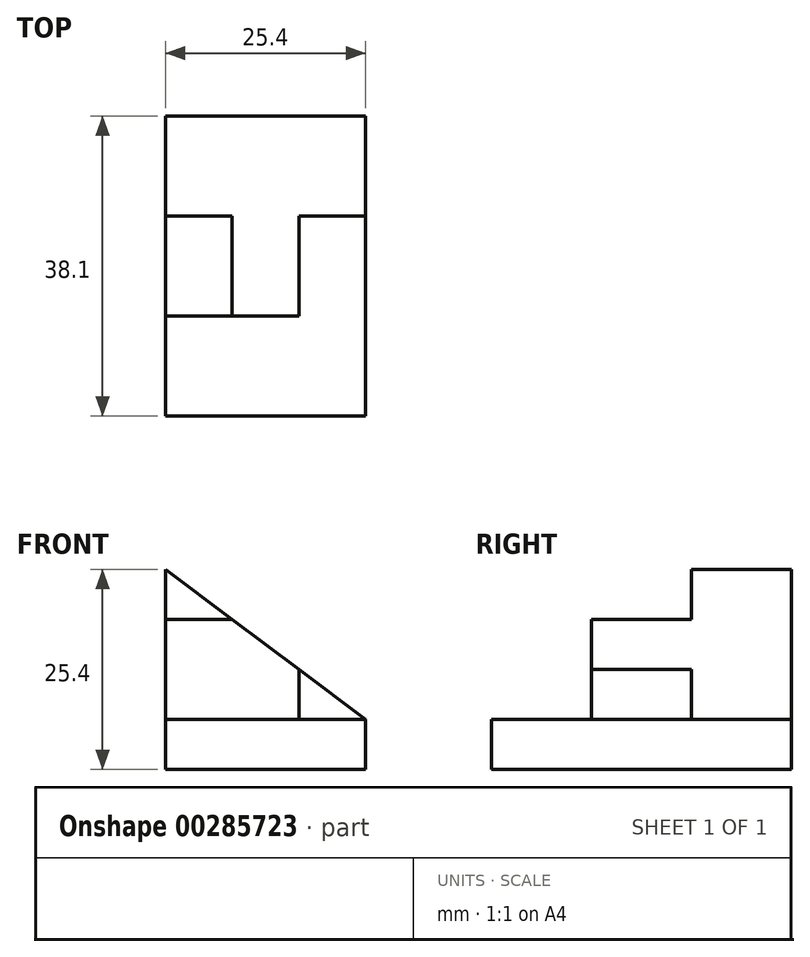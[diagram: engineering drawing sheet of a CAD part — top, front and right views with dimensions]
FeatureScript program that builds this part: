
annotation { "Feature Type Name" : "Feature", "Feature Type Description" : "" }
export const myFeature = defineFeature(function(context is Context, id is Id, definition is map)
    precondition{}
    {
        {
            var Q0;
            Q0=qCreatedBy(makeId("Front.planeOp"),FACE);
            var sketch = newSketch(context, id + "F0", { "sketchPlane" : qUnion([Q0])});
            skLineSegment(sketch, "E0", {"start": v(0, 0) * mm, "end": v(25.4, 0) * mm});
            skLineSegment(sketch, "E1", {"start": v(25.4, 0) * mm, "end": v(25.4, 6.35) * mm});
            skLineSegment(sketch, "E2", {"start": v(25.4, 6.35) * mm, "end": v(0, 6.35) * mm});
            skLineSegment(sketch, "E3", {"start": v(0, 6.35) * mm, "end": v(0, 0) * mm});
            skLineSegment(sketch, "E4", {"start": v(25.4, 6.35) * mm, "end": v(0, 25.4) * mm});
            skLineSegment(sketch, "E5", {"start": v(0, 25.4) * mm, "end": v(0, 6.35) * mm});
            skLineSegment(sketch, "E6", {"start": v(0, 19.05) * mm, "end": v(8.47, 19.05) * mm});
            skLineSegment(sketch, "E7", {"start": v(16.93, 6.35) * mm, "end": v(16.93, 12.7) * mm});
            skLineSegment(sketch, "E8", {"start": v(16.93, 12.7) * mm, "end": v(0, 12.7) * mm});
            skSolve(sketch);
        }
        {
            var Q0;
            {var subQ3=sQuery(id+"F0.wireOp",EDGE,"E6");Q0=makeQuery(id+"F0.imprint","IMPRINT",FACE,{"disambiguationData":[TD([[makeQuery(id+"F0.imprint","IMPRINT",EDGE,{"derivedFrom":subQ3}),1.0]])]});}
            extrude(context, id + "F1", {"entities" : qUnion([Q0]), "depth" : 12.7 * mm});
        }
        {
            var Q0;
            {var subQ0=sQuery(id+"F0.wireOp",EDGE,"E6");Q0=makeQuery(id+"F0.imprint","IMPRINT",FACE,{"disambiguationData":[TD([[makeQuery(id+"F0.imprint","IMPRINT",EDGE,{"derivedFrom":subQ0}),-1.0]])]});}
            extrude(context, id + "F2", {"entities" : qUnion([Q0]), "operationType" : NewBodyOperationType.ADD, "depth" : 25.4 * mm});
        }
        {
            var Q0;
            {var subQ3=sQuery(id+"F0.wireOp",EDGE,"E7");Q0=makeQuery(id+"F0.imprint","IMPRINT",FACE,{"disambiguationData":[TD([[makeQuery(id+"F0.imprint","IMPRINT",EDGE,{"derivedFrom":subQ3}),1.0]])]});}
            extrude(context, id + "F3", {"entities" : qUnion([Q0]), "operationType" : NewBodyOperationType.ADD, "depth" : 25.4 * mm});
        }
        {
            var Q0;
            {var subQ3=sQuery(id+"F0.wireOp",EDGE,"E7");Q0=makeQuery(id+"F0.imprint","IMPRINT",FACE,{"disambiguationData":[TD([[makeQuery(id+"F0.imprint","IMPRINT",EDGE,{"derivedFrom":subQ3}),-1.0]])]});}
            extrude(context, id + "F4", {"entities" : qUnion([Q0]), "operationType" : NewBodyOperationType.ADD, "depth" : 12.7 * mm});
        }
        {
            var Q0;
            Q0=makeQuery(id+"F0.imprint","IMPRINT",FACE,{"disambiguationData":[TD([[makeQuery(id+"F0.imprint","IMPRINT",EDGE,{"derivedFrom":sQuery(id+"F0.wireOp",EDGE,"E0")}),1.0]])]});
            extrude(context, id + "F5", {"entities" : qUnion([Q0]), "operationType" : NewBodyOperationType.ADD, "depth" : 38.1 * mm});
        }
    });
